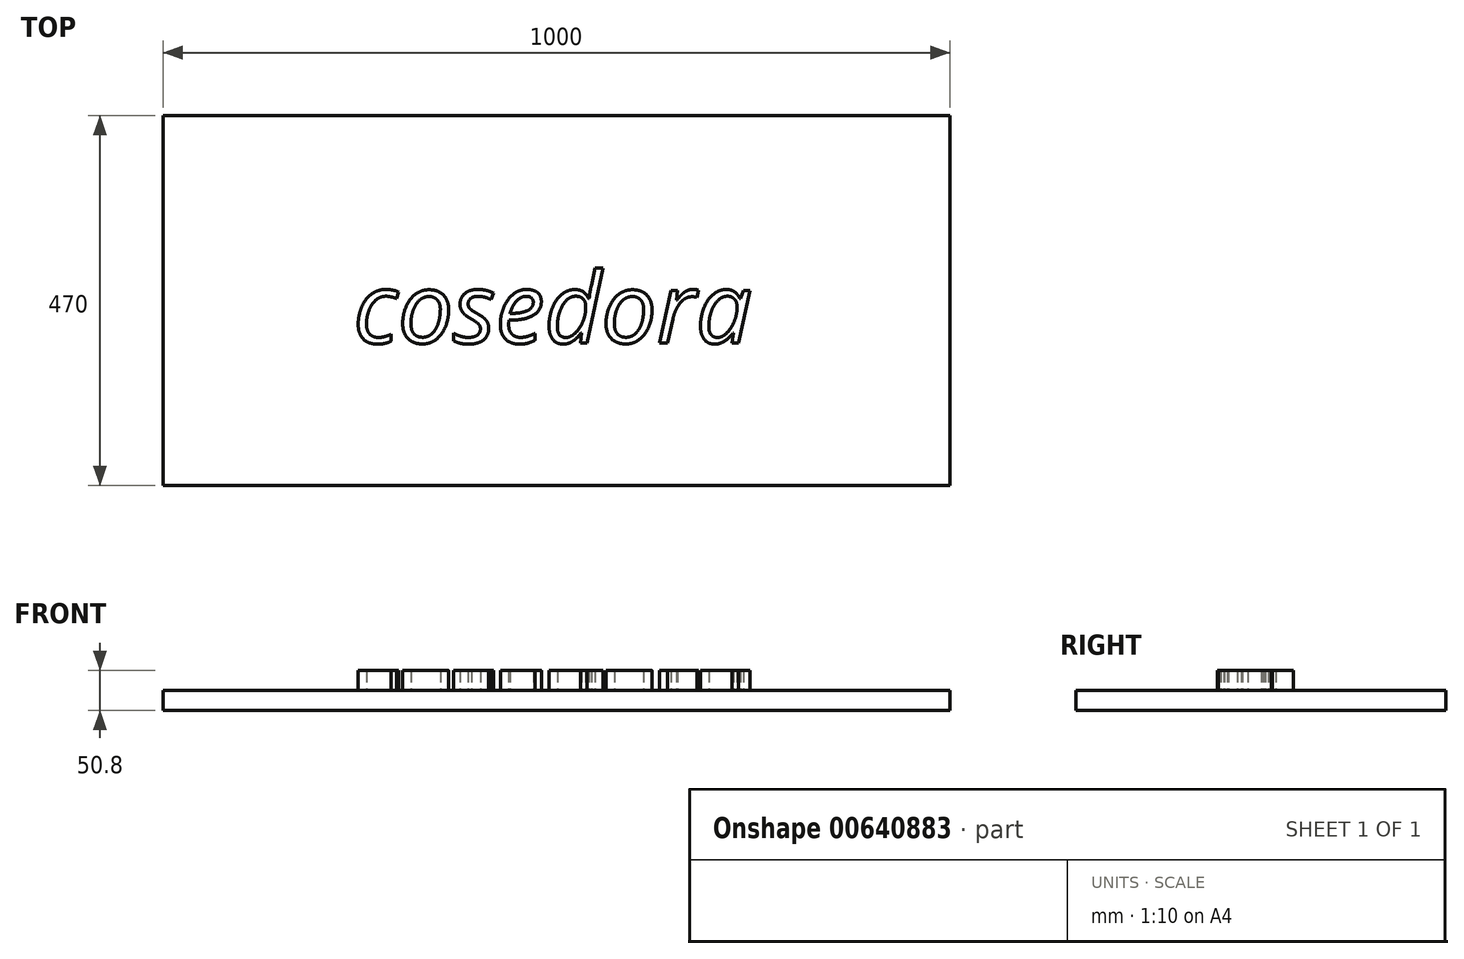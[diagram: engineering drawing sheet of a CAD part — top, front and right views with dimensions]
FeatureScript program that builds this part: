
annotation { "Feature Type Name" : "Feature", "Feature Type Description" : "" }
export const myFeature = defineFeature(function(context is Context, id is Id, definition is map)
    precondition{}
    {
        {
            var Q0;
            Q0=qCreatedBy(makeId("Top.planeOp"),FACE);
            var sketch = newSketch(context, id + "F0", { "sketchPlane" : qUnion([Q0])});
            skLineSegment(sketch, "E0.bottom", {"start": v(-497.84, 328.27) * mm, "end": v(502.16, 328.27) * mm});
            skLineSegment(sketch, "E0.top", {"start": v(-497.84, -141.73) * mm, "end": v(502.16, -141.73) * mm});
            skLineSegment(sketch, "E0.left", {"start": v(-497.84, 328.27) * mm, "end": v(-497.84, -141.73) * mm});
            skLineSegment(sketch, "E0.right", {"start": v(502.16, 328.27) * mm, "end": v(502.16, -141.73) * mm});
            skSolve(sketch);
        }
        {
            var Q0;
            Q0 = qSketchRegion(id + "F0", true);
            extrude(context, id + "F1", {"entities" : qUnion([Q0]), "depth" : 25.4 * mm, "offsetDistance" : 25.4 * mm});
        }
        {
            var Q0;
            Q0=makeQuery(id+"F1.opExtrude","CAP_FACE",FACE,{"disambiguationData":[OSD([sQuery(id+"F0.wireOp",EDGE,"E0.bottom"),sQuery(id+"F0.wireOp",EDGE,"E0.top"),sQuery(id+"F0.wireOp",EDGE,"E0.left"),sQuery(id+"F0.wireOp",EDGE,"E0.right")])],"isStart":false});
            var sketch = newSketch(context, id + "F2", { "sketchPlane" : qUnion([Q0])});
            skText(sketch, "E1", { "text": "cosedora ", "fontName": "OpenSans-Italic.ttf"});
            const initialGuessF2  = {"E1": [-0.25573, 0.03895, 1, 0, 0.0903]};
            skSetInitialGuess(sketch, initialGuessF2);
            skSolve(sketch);
        }
        {
            var Q0;
            Q0 = qSketchRegion(id + "F2", true);
            extrude(context, id + "F3", {"entities" : qUnion([Q0]), "operationType" : NewBodyOperationType.ADD, "depth" : 25.4 * mm, "offsetDistance" : 25.4 * mm});
        }
    });
